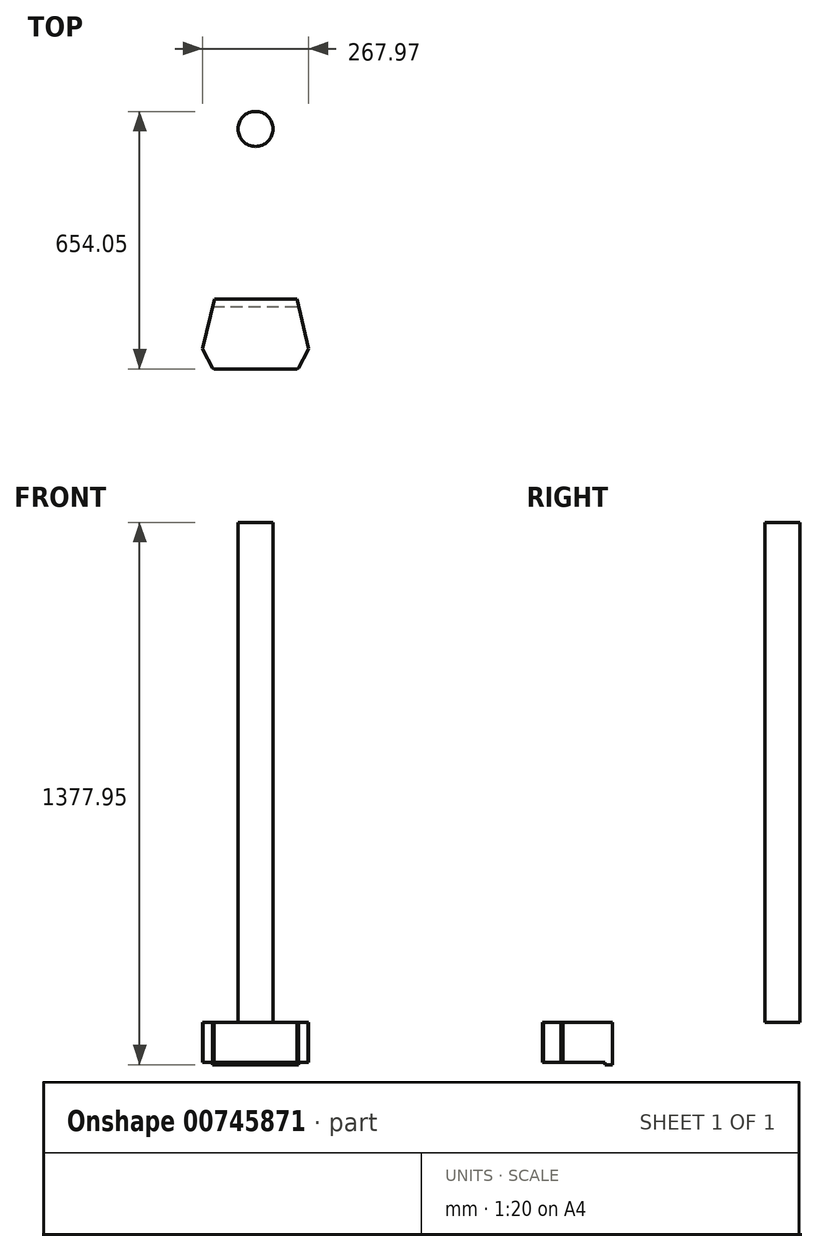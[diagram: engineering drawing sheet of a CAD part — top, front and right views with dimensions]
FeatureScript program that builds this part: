
annotation { "Feature Type Name" : "Feature", "Feature Type Description" : "" }
export const myFeature = defineFeature(function(context is Context, id is Id, definition is map)
    precondition{}
    {
        {
            var Q0;
            Q0=qCreatedBy(makeId("Top.planeOp"),FACE);
            var sketch = newSketch(context, id + "F0", { "sketchPlane" : qUnion([Q0])});
            skLineSegment(sketch, "E0", {"start": v(-153.63, -90.08) * mm, "end": v(138.47, -90.08) * mm});
            skLineSegment(sketch, "E1", {"start": v(138.47, -90.08) * mm, "end": v(97.2, 87.72) * mm});
            skLineSegment(sketch, "E2", {"start": v(97.2, 87.72) * mm, "end": v(-112.35, 87.72) * mm});
            skLineSegment(sketch, "E3", {"start": v(-112.35, 87.72) * mm, "end": v(-153.63, -90.08) * mm});
            skSolve(sketch);
        }
        {
            var Q0;
            Q0=makeQuery(id+"F0.imprint","IMPRINT",FACE,{"disambiguationData":[TD([[makeQuery(id+"F0.imprint","IMPRINT",EDGE,{"derivedFrom":sQuery(id+"F0.wireOp",EDGE,"E0")}),1.0]])]});
            extrude(context, id + "F1", {"entities" : qUnion([Q0]), "depth" : 107.95 * mm, "offsetDistance" : 25.4 * mm});
        }
        {
            var Q0;
            Q0=makeQuery(id+"F1.opExtrude","CAP_FACE",FACE,{"disambiguationData":[OSD([sQuery(id+"F0.wireOp",EDGE,"E0"),sQuery(id+"F0.wireOp",EDGE,"E1"),sQuery(id+"F0.wireOp",EDGE,"E2"),sQuery(id+"F0.wireOp",EDGE,"E3")])],"isStart":true});
            var sketch = newSketch(context, id + "F2", { "sketchPlane" : qUnion([Q0])});
            skLineSegment(sketch, "E4", {"start": v(-153.63, 90.08) * mm, "end": v(138.47, 90.08) * mm});
            skLineSegment(sketch, "E5", {"start": v(-116.77, -68.67) * mm, "end": v(101.62, -68.67) * mm});
            skLineSegment(sketch, "E6", {"start": v(138.47, 90.08) * mm, "end": v(101.62, -68.67) * mm});
            skLineSegment(sketch, "E7", {"start": v(-153.63, 90.08) * mm, "end": v(-116.77, -68.67) * mm});
            skSolve(sketch);
        }
        {
            var Q0;
            Q0 = qSketchRegion(id + "F2", true);
            extrude(context, id + "F3", {"entities" : qUnion([Q0]), "operationType" : NewBodyOperationType.REMOVE, "oppositeDirection" : true, "depth" : 6.35 * mm, "offsetDistance" : 25.4 * mm});
        }
        {
            var Q0;
            Q0=makeQuery(id+"F1.opExtrude","SWEPT_EDGE",EDGE,{"disambiguationData":[OSD([sQuery(id+"F0.wireOp",EDGE,"E0"),sQuery(id+"F0.wireOp",EDGE,"E1")])]});
            var Q1;
            Q1=makeQuery(id+"F1.opExtrude","SWEPT_EDGE",EDGE,{"disambiguationData":[OSD([sQuery(id+"F0.wireOp",EDGE,"E0"),sQuery(id+"F0.wireOp",EDGE,"E3")])]});
            chamfer(context, id + "F4", {"entities" : qUnion([Q0, Q1]), "chamferType" : ChamferType.TWO_OFFSETS, "width1" : 38.1 * mm, "oppositeDirection" : false, "width2" : 50.8 * mm, "tangentPropagation" : true});
        }
        {
            var Q0;
            {var subQ0=sQuery(id+"F0.wireOp",EDGE,"E0");Q0=makeQuery(id+"F4.opChamfer","BLEND_EDGE",EDGE,{"blendedFrom":[makeQuery(id+"F1.opExtrude","SWEPT_EDGE",EDGE,{"disambiguationData":[OSD([subQ0,sQuery(id+"F0.wireOp",EDGE,"E1")])]}),makeQuery(id+"F1.opExtrude","SWEPT_FACE",FACE,{"disambiguationData":[OSD([subQ0])]})],"blendedInto":[makeQuery(id+"F1.opExtrude","SWEPT_FACE",FACE,{"disambiguationData":[OSD([subQ0])]})]});}
            var Q1;
            {var subQ0=sQuery(id+"F0.wireOp",EDGE,"E1");Q1=makeQuery(id+"F4.opChamfer","BLEND_EDGE",EDGE,{"blendedFrom":[makeQuery(id+"F1.opExtrude","SWEPT_EDGE",EDGE,{"disambiguationData":[OSD([sQuery(id+"F0.wireOp",EDGE,"E0"),subQ0])]}),makeQuery(id+"F1.opExtrude","SWEPT_FACE",FACE,{"disambiguationData":[OSD([subQ0])]})],"blendedInto":[makeQuery(id+"F1.opExtrude","SWEPT_FACE",FACE,{"disambiguationData":[OSD([subQ0])]})]});}
            var Q2;
            {var subQ0=sQuery(id+"F0.wireOp",EDGE,"E0");Q2=makeQuery(id+"F4.opChamfer","BLEND_EDGE",EDGE,{"blendedFrom":[makeQuery(id+"F1.opExtrude","SWEPT_EDGE",EDGE,{"disambiguationData":[OSD([subQ0,sQuery(id+"F0.wireOp",EDGE,"E3")])]}),makeQuery(id+"F1.opExtrude","SWEPT_FACE",FACE,{"disambiguationData":[OSD([subQ0])]})],"blendedInto":[makeQuery(id+"F1.opExtrude","SWEPT_FACE",FACE,{"disambiguationData":[OSD([subQ0])]})]});}
            var Q3;
            {var subQ0=sQuery(id+"F0.wireOp",EDGE,"E3");Q3=makeQuery(id+"F4.opChamfer","BLEND_EDGE",EDGE,{"blendedFrom":[makeQuery(id+"F1.opExtrude","SWEPT_EDGE",EDGE,{"disambiguationData":[OSD([sQuery(id+"F0.wireOp",EDGE,"E0"),subQ0])]}),makeQuery(id+"F1.opExtrude","SWEPT_FACE",FACE,{"disambiguationData":[OSD([subQ0])]})],"blendedInto":[makeQuery(id+"F1.opExtrude","SWEPT_FACE",FACE,{"disambiguationData":[OSD([subQ0])]})]});}
            chamfer(context, id + "F5", {"entities" : qUnion([Q0, Q1, Q2, Q3]), "width" : 2.54 * mm, "tangentPropagation" : true});
        }
        {
            var Q0;
            Q0=makeQuery(id+"F1.opExtrude","CAP_FACE",FACE,{"disambiguationData":[OSD([sQuery(id+"F0.wireOp",EDGE,"E0"),sQuery(id+"F0.wireOp",EDGE,"E1"),sQuery(id+"F0.wireOp",EDGE,"E2"),sQuery(id+"F0.wireOp",EDGE,"E3")])],"isStart":false});
            var sketch = newSketch(context, id + "F6", { "sketchPlane" : qUnion([Q0])});
            skLineSegment(sketch, "E8.bottom", {"start": v(-617.18, 1129.12) * mm, "end": v(602.02, 1129.12) * mm, "construction": true});
            skLineSegment(sketch, "E8.top", {"start": v(-617.18, -90.08) * mm, "end": v(602.02, -90.08) * mm, "construction": true});
            skLineSegment(sketch, "E8.left", {"start": v(-617.18, 1129.12) * mm, "end": v(-617.18, -90.08) * mm, "construction": true});
            skLineSegment(sketch, "E8.right", {"start": v(602.02, 1129.12) * mm, "end": v(602.02, -90.08) * mm, "construction": true});
            skCircle(sketch, "E9", {"center": v(-7.58, 519.52) * mm, "radius": 44.45 * mm});
            skSolve(sketch);
        }
        {
            var Q0;
            Q0 = qSketchRegion(id + "F6", true);
            extrude(context, id + "F7", {"entities" : qUnion([Q0]), "depth" : 1270 * mm, "offsetDistance" : 25.4 * mm});
        }
        {
            var Q0;
            Q0 = qSketchRegion(id + "F6", true);
            extrude(context, id + "F8", {"entities" : qUnion([Q0]), "operationType" : NewBodyOperationType.ADD, "depth" : 25.4 * mm, "offsetDistance" : 25.4 * mm});
        }
    });
